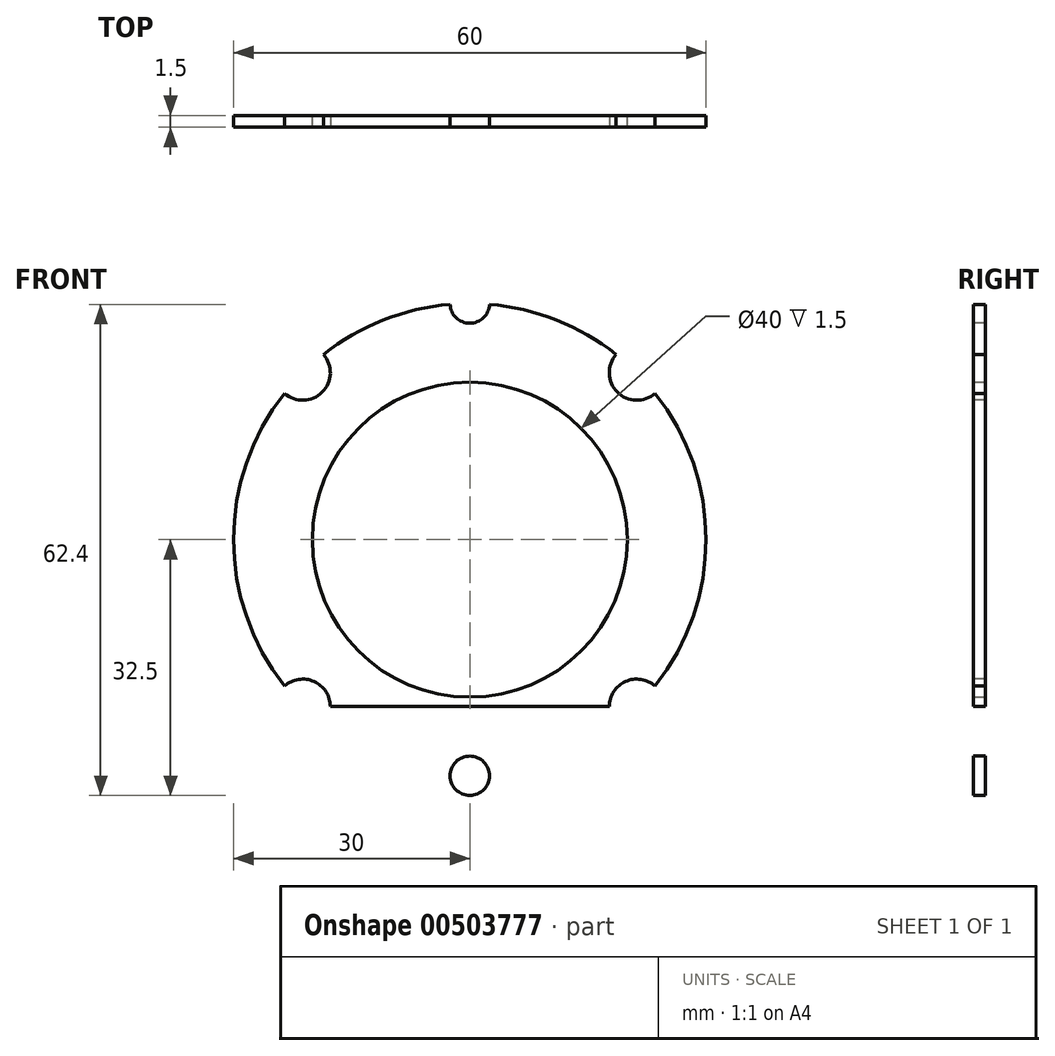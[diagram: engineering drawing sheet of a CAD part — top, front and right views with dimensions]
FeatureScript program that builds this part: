
annotation { "Feature Type Name" : "Feature", "Feature Type Description" : "" }
export const myFeature = defineFeature(function(context is Context, id is Id, definition is map)
    precondition{}
    {
        {
            var Q0;
            Q0=qCreatedBy(makeId("Front.planeOp"),FACE);
            var sketch = newSketch(context, id + "F0", { "sketchPlane" : qUnion([Q0])});
            skCircle(sketch, "E0", {"center": v(0, 0) * mm, "radius": 170.5 * mm});
            skCircle(sketch, "E1", {"center": v(0, 0) * mm, "radius": 20 * mm});
            skCircle(sketch, "E2.cCircle", {"center": v(0, 0) * mm, "radius": 21.21 * mm, "construction": true});
            skLineSegment(sketch, "E2.0", {"start": v(30, 0) * mm, "end": v(0, -30) * mm});
            skLineSegment(sketch, "E2.1", {"start": v(0, -30) * mm, "end": v(-30, 0) * mm});
            skLineSegment(sketch, "E2.2", {"start": v(-30, 0) * mm, "end": v(0, 30) * mm});
            skLineSegment(sketch, "E2.3", {"start": v(0, 30) * mm, "end": v(30, 0) * mm});
            skPoint(sketch, "E2.0.midPoint", {"position": v(15, -15) * mm});
            skLineSegment(sketch, "E3", {"start": v(0, 0) * mm, "end": v(21.21, -21.21) * mm});
            skLineSegment(sketch, "E4", {"start": v(0, 0) * mm, "end": v(-21.21, 21.21) * mm});
            skSolve(sketch);
        }
        {
            var Q0;
            {var subQ0=sQuery(id+"F0.wireOp",EDGE,"E2.3");Q0=makeQuery(id+"F0.imprint","IMPRINT",FACE,{"disambiguationData":[TD([[makeQuery(id+"F0.imprint","IMPRINT",EDGE,{"derivedFrom":subQ0}),-1.0]])]});}
            var Q1;
            {var subQ0=sQuery(id+"F0.wireOp",EDGE,"E2.1");Q1=makeQuery(id+"F0.imprint","IMPRINT",FACE,{"disambiguationData":[TD([[makeQuery(id+"F0.imprint","IMPRINT",EDGE,{"derivedFrom":subQ0}),-1.0]])]});}
            var Q2;
            Q2=makeQuery(id+"F0.imprint","IMPRINT",FACE,{"disambiguationData":[TD([[makeQuery(id+"F0.imprint","IMPRINT",EDGE,{"derivedFrom":sQuery(id+"F0.wireOp",EDGE,"E0")}),1.0]])]});
            extrude(context, id + "F1", {"entities" : qUnion([Q0, Q1, Q2]), "depth" : 1.5 * mm});
        }
        {
            var Q0;
            Q0=makeQuery(id+"F1.opExtrude","CAP_FACE",FACE,{"disambiguationData":[OSD([sQuery(id+"F0.wireOp",EDGE,"E0"),sQuery(id+"F0.wireOp",EDGE,"E1")])],"isStart":false});
            var sketch = newSketch(context, id + "F2", { "sketchPlane" : qUnion([Q0])});
            skCircle(sketch, "E5.cCircle", {"center": v(0, 0) * mm, "radius": 21.21 * mm, "construction": true});
            skLineSegment(sketch, "E5.0", {"start": v(-21.21, 21.21) * mm, "end": v(21.21, 21.21) * mm});
            skLineSegment(sketch, "E5.1", {"start": v(21.21, 21.21) * mm, "end": v(21.21, -21.21) * mm});
            skLineSegment(sketch, "E5.2", {"start": v(21.21, -21.21) * mm, "end": v(-21.21, -21.21) * mm});
            skLineSegment(sketch, "E5.3", {"start": v(-21.21, -21.21) * mm, "end": v(-21.21, 21.21) * mm});
            skPoint(sketch, "E5.0.midPoint", {"position": v(0, 21.21) * mm});
            skCircle(sketch, "E6", {"center": v(0, 0) * mm, "radius": 30 * mm});
            skPoint(sketch, "E7", {"position": v(0, 30) * mm});
            skPoint(sketch, "E8", {"position": v(0, -30) * mm});
            skCircle(sketch, "E9", {"center": v(0, 30) * mm, "radius": 2.5 * mm});
            skCircle(sketch, "E10", {"center": v(0, -30) * mm, "radius": 2.5 * mm});
            skCircle(sketch, "E11", {"center": v(21.21, 21.21) * mm, "radius": 3.5 * mm});
            skCircle(sketch, "E12", {"center": v(-21.21, 21.21) * mm, "radius": 3.5 * mm});
            skCircle(sketch, "E13", {"center": v(-21.21, -21.21) * mm, "radius": 3.5 * mm});
            skCircle(sketch, "E14", {"center": v(21.21, -21.21) * mm, "radius": 3.5 * mm});
            skSolve(sketch);
        }
        {
            var Q0;
            {var subQ1=sQuery(id+"F2.wireOp",EDGE,"E5.0");var subQ3=sQuery(id+"F2.wireOp",EDGE,"E12");var subQ4=makeQuery(id+"F2.imprint","INTERSECT",VERTEX,{"derivedFrom":[subQ1,subQ3]});Q0=makeQuery(id+"F2.imprint","IMPRINT",FACE,{"disambiguationData":[TD([[makeQuery(id+"F2.imprint","IMPRINT",EDGE,{"disambiguationData":[TD([[subQ4,1.0]])],"derivedFrom":subQ3}),1.0]])]});}
            var Q1;
            {var subQ0=sQuery(id+"F2.wireOp",EDGE,"E6");var subQ2=sQuery(id+"F2.wireOp",EDGE,"E12");var subQ3=makeQuery(id+"F2.imprint","INTERSECT",VERTEX,{"disambiguationData":[OD(0.0)],"derivedFrom":[subQ0,subQ2]});Q1=makeQuery(id+"F2.imprint","IMPRINT",FACE,{"disambiguationData":[TD([[makeQuery(id+"F2.imprint","IMPRINT",EDGE,{"disambiguationData":[TD([[subQ3,-1.0]])],"derivedFrom":subQ2}),1.0]])]});}
            var Q2;
            {var subQ1=sQuery(id+"F2.wireOp",EDGE,"E5.3");var subQ3=sQuery(id+"F2.wireOp",EDGE,"E12");var subQ4=makeQuery(id+"F2.imprint","INTERSECT",VERTEX,{"derivedFrom":[subQ1,subQ3]});Q2=makeQuery(id+"F2.imprint","IMPRINT",FACE,{"disambiguationData":[TD([[makeQuery(id+"F2.imprint","IMPRINT",EDGE,{"disambiguationData":[TD([[subQ4,1.0]])],"derivedFrom":subQ3}),1.0]])]});}
            var Q3;
            {var subQ1=sQuery(id+"F2.wireOp",EDGE,"E5.0");var subQ3=sQuery(id+"F2.wireOp",EDGE,"E12");var subQ4=makeQuery(id+"F2.imprint","INTERSECT",VERTEX,{"derivedFrom":[subQ1,subQ3]});Q3=makeQuery(id+"F2.imprint","IMPRINT",FACE,{"disambiguationData":[TD([[makeQuery(id+"F2.imprint","IMPRINT",EDGE,{"disambiguationData":[TD([[subQ4,-1.0]])],"derivedFrom":subQ3}),1.0]])]});}
            var Q4;
            {var subQ0=sQuery(id+"F2.wireOp",EDGE,"E6");var subQ2=sQuery(id+"F2.wireOp",EDGE,"E13");var subQ3=makeQuery(id+"F2.imprint","INTERSECT",VERTEX,{"disambiguationData":[OD(0.0)],"derivedFrom":[subQ0,subQ2]});Q4=makeQuery(id+"F2.imprint","IMPRINT",FACE,{"disambiguationData":[TD([[makeQuery(id+"F2.imprint","IMPRINT",EDGE,{"disambiguationData":[TD([[subQ3,-1.0]])],"derivedFrom":subQ2}),1.0]])]});}
            var Q5;
            {var subQ1=sQuery(id+"F2.wireOp",EDGE,"E5.3");var subQ3=sQuery(id+"F2.wireOp",EDGE,"E13");var subQ4=makeQuery(id+"F2.imprint","INTERSECT",VERTEX,{"derivedFrom":[subQ1,subQ3]});Q5=makeQuery(id+"F2.imprint","IMPRINT",FACE,{"disambiguationData":[TD([[makeQuery(id+"F2.imprint","IMPRINT",EDGE,{"disambiguationData":[TD([[subQ4,-1.0]])],"derivedFrom":subQ3}),1.0]])]});}
            var Q6;
            {var subQ1=sQuery(id+"F2.wireOp",EDGE,"E5.2");var subQ3=sQuery(id+"F2.wireOp",EDGE,"E13");var subQ4=makeQuery(id+"F2.imprint","INTERSECT",VERTEX,{"derivedFrom":[subQ1,subQ3]});Q6=makeQuery(id+"F2.imprint","IMPRINT",FACE,{"disambiguationData":[TD([[makeQuery(id+"F2.imprint","IMPRINT",EDGE,{"disambiguationData":[TD([[subQ4,-1.0]])],"derivedFrom":subQ3}),1.0]])]});}
            var Q7;
            {var subQ1=sQuery(id+"F2.wireOp",EDGE,"E5.2");var subQ3=sQuery(id+"F2.wireOp",EDGE,"E13");var subQ4=makeQuery(id+"F2.imprint","INTERSECT",VERTEX,{"derivedFrom":[subQ1,subQ3]});Q7=makeQuery(id+"F2.imprint","IMPRINT",FACE,{"disambiguationData":[TD([[makeQuery(id+"F2.imprint","IMPRINT",EDGE,{"disambiguationData":[TD([[subQ4,1.0]])],"derivedFrom":subQ3}),1.0]])]});}
            var Q8;
            {var subQ0=sQuery(id+"F2.wireOp",EDGE,"E10");var subQ1=sQuery(id+"F2.wireOp",EDGE,"E6");var subQ2=makeQuery(id+"F2.imprint","INTERSECT",VERTEX,{"disambiguationData":[OD(0.0)],"derivedFrom":[subQ1,subQ0]});Q8=makeQuery(id+"F2.imprint","IMPRINT",FACE,{"disambiguationData":[TD([[makeQuery(id+"F2.imprint","IMPRINT",EDGE,{"disambiguationData":[TD([[subQ2,-1.0]])],"derivedFrom":subQ1}),1.0]])]});}
            var Q9;
            {var subQ0=sQuery(id+"F2.wireOp",EDGE,"E10");var subQ1=sQuery(id+"F2.wireOp",EDGE,"E6");var subQ2=makeQuery(id+"F2.imprint","INTERSECT",VERTEX,{"disambiguationData":[OD(0.0)],"derivedFrom":[subQ1,subQ0]});Q9=makeQuery(id+"F2.imprint","IMPRINT",FACE,{"disambiguationData":[TD([[makeQuery(id+"F2.imprint","IMPRINT",EDGE,{"disambiguationData":[TD([[subQ2,-1.0]])],"derivedFrom":subQ1}),-1.0]])]});}
            var Q10;
            {var subQ0=sQuery(id+"F2.wireOp",EDGE,"E6");var subQ2=sQuery(id+"F2.wireOp",EDGE,"E14");var subQ3=makeQuery(id+"F2.imprint","INTERSECT",VERTEX,{"disambiguationData":[OD(0.0)],"derivedFrom":[subQ0,subQ2]});Q10=makeQuery(id+"F2.imprint","IMPRINT",FACE,{"disambiguationData":[TD([[makeQuery(id+"F2.imprint","IMPRINT",EDGE,{"disambiguationData":[TD([[subQ3,-1.0]])],"derivedFrom":subQ2}),1.0]])]});}
            var Q11;
            {var subQ1=sQuery(id+"F2.wireOp",EDGE,"E5.1");var subQ3=sQuery(id+"F2.wireOp",EDGE,"E14");var subQ4=makeQuery(id+"F2.imprint","INTERSECT",VERTEX,{"derivedFrom":[subQ1,subQ3]});Q11=makeQuery(id+"F2.imprint","IMPRINT",FACE,{"disambiguationData":[TD([[makeQuery(id+"F2.imprint","IMPRINT",EDGE,{"disambiguationData":[TD([[subQ4,-1.0]])],"derivedFrom":subQ3}),1.0]])]});}
            var Q12;
            {var subQ1=sQuery(id+"F2.wireOp",EDGE,"E5.2");var subQ3=sQuery(id+"F2.wireOp",EDGE,"E14");var subQ4=makeQuery(id+"F2.imprint","INTERSECT",VERTEX,{"derivedFrom":[subQ1,subQ3]});Q12=makeQuery(id+"F2.imprint","IMPRINT",FACE,{"disambiguationData":[TD([[makeQuery(id+"F2.imprint","IMPRINT",EDGE,{"disambiguationData":[TD([[subQ4,-1.0]])],"derivedFrom":subQ3}),1.0]])]});}
            var Q13;
            {var subQ1=sQuery(id+"F2.wireOp",EDGE,"E5.1");var subQ3=sQuery(id+"F2.wireOp",EDGE,"E14");var subQ4=makeQuery(id+"F2.imprint","INTERSECT",VERTEX,{"derivedFrom":[subQ1,subQ3]});Q13=makeQuery(id+"F2.imprint","IMPRINT",FACE,{"disambiguationData":[TD([[makeQuery(id+"F2.imprint","IMPRINT",EDGE,{"disambiguationData":[TD([[subQ4,1.0]])],"derivedFrom":subQ3}),1.0]])]});}
            var Q14;
            {var subQ1=sQuery(id+"F2.wireOp",EDGE,"E5.0");var subQ3=sQuery(id+"F2.wireOp",EDGE,"E11");var subQ4=makeQuery(id+"F2.imprint","INTERSECT",VERTEX,{"derivedFrom":[subQ1,subQ3]});Q14=makeQuery(id+"F2.imprint","IMPRINT",FACE,{"disambiguationData":[TD([[makeQuery(id+"F2.imprint","IMPRINT",EDGE,{"disambiguationData":[TD([[subQ4,-1.0]])],"derivedFrom":subQ3}),1.0]])]});}
            var Q15;
            {var subQ1=sQuery(id+"F2.wireOp",EDGE,"E5.0");var subQ3=sQuery(id+"F2.wireOp",EDGE,"E11");var subQ4=makeQuery(id+"F2.imprint","INTERSECT",VERTEX,{"derivedFrom":[subQ1,subQ3]});Q15=makeQuery(id+"F2.imprint","IMPRINT",FACE,{"disambiguationData":[TD([[makeQuery(id+"F2.imprint","IMPRINT",EDGE,{"disambiguationData":[TD([[subQ4,1.0]])],"derivedFrom":subQ3}),1.0]])]});}
            var Q16;
            {var subQ1=sQuery(id+"F2.wireOp",EDGE,"E5.1");var subQ3=sQuery(id+"F2.wireOp",EDGE,"E11");var subQ4=makeQuery(id+"F2.imprint","INTERSECT",VERTEX,{"derivedFrom":[subQ1,subQ3]});Q16=makeQuery(id+"F2.imprint","IMPRINT",FACE,{"disambiguationData":[TD([[makeQuery(id+"F2.imprint","IMPRINT",EDGE,{"disambiguationData":[TD([[subQ4,-1.0]])],"derivedFrom":subQ3}),1.0]])]});}
            var Q17;
            {var subQ0=sQuery(id+"F2.wireOp",EDGE,"E6");var subQ2=sQuery(id+"F2.wireOp",EDGE,"E11");var subQ3=makeQuery(id+"F2.imprint","INTERSECT",VERTEX,{"disambiguationData":[OD(0.0)],"derivedFrom":[subQ0,subQ2]});Q17=makeQuery(id+"F2.imprint","IMPRINT",FACE,{"disambiguationData":[TD([[makeQuery(id+"F2.imprint","IMPRINT",EDGE,{"disambiguationData":[TD([[subQ3,-1.0]])],"derivedFrom":subQ2}),1.0]])]});}
            var Q18;
            {var subQ0=sQuery(id+"F2.wireOp",EDGE,"E9");var subQ1=sQuery(id+"F2.wireOp",EDGE,"E6");var subQ2=makeQuery(id+"F2.imprint","INTERSECT",VERTEX,{"disambiguationData":[OD(0.0)],"derivedFrom":[subQ1,subQ0]});Q18=makeQuery(id+"F2.imprint","IMPRINT",FACE,{"disambiguationData":[TD([[makeQuery(id+"F2.imprint","IMPRINT",EDGE,{"disambiguationData":[TD([[subQ2,-1.0]])],"derivedFrom":subQ1}),1.0]])]});}
            var Q19;
            {var subQ0=sQuery(id+"F2.wireOp",EDGE,"E9");var subQ1=sQuery(id+"F2.wireOp",EDGE,"E6");var subQ2=makeQuery(id+"F2.imprint","INTERSECT",VERTEX,{"disambiguationData":[OD(0.0)],"derivedFrom":[subQ1,subQ0]});Q19=makeQuery(id+"F2.imprint","IMPRINT",FACE,{"disambiguationData":[TD([[makeQuery(id+"F2.imprint","IMPRINT",EDGE,{"disambiguationData":[TD([[subQ2,-1.0]])],"derivedFrom":subQ1}),-1.0]])]});}
            extrude(context, id + "F3", {"entities" : qUnion([Q0, Q1, Q2, Q3, Q4, Q5, Q6, Q7, Q8, Q9, Q10, Q11, Q12, Q13, Q14, Q15, Q16, Q17, Q18, Q19]), "operationType" : NewBodyOperationType.REMOVE, "oppositeDirection" : true, "depth" : 25 * mm});
        }
        {
            var Q0;
            Q0=makeQuery(id+"F1.opExtrude","CAP_FACE",FACE,{"disambiguationData":[OSD([sQuery(id+"F0.wireOp",EDGE,"E0"),sQuery(id+"F0.wireOp",EDGE,"E1")])],"isStart":false});
            var sketch = newSketch(context, id + "F4", { "sketchPlane" : qUnion([Q0])});
            skCircle(sketch, "E15.cCircle", {"center": v(0, 0) * mm, "radius": 92.39 * mm, "construction": true});
            skLineSegment(sketch, "E15.0", {"start": v(38.27, -92.39) * mm, "end": v(-38.27, -92.39) * mm});
            skLineSegment(sketch, "E15.1", {"start": v(-38.27, -92.39) * mm, "end": v(-92.39, -38.27) * mm});
            skLineSegment(sketch, "E15.2", {"start": v(-92.39, -38.27) * mm, "end": v(-92.39, 38.27) * mm});
            skLineSegment(sketch, "E15.3", {"start": v(-92.39, 38.27) * mm, "end": v(-38.27, 92.39) * mm});
            skLineSegment(sketch, "E15.4", {"start": v(-38.27, 92.39) * mm, "end": v(38.27, 92.39) * mm});
            skLineSegment(sketch, "E15.5", {"start": v(38.27, 92.39) * mm, "end": v(92.39, 38.27) * mm});
            skLineSegment(sketch, "E15.6", {"start": v(92.39, 38.27) * mm, "end": v(92.39, -38.27) * mm});
            skLineSegment(sketch, "E15.7", {"start": v(92.39, -38.27) * mm, "end": v(38.27, -92.39) * mm});
            skPoint(sketch, "E15.0.midPoint", {"position": v(0, -92.39) * mm});
            skCircle(sketch, "E16", {"center": v(-38.27, 92.39) * mm, "radius": 12.5 * mm});
            skCircle(sketch, "E17", {"center": v(38.27, 92.39) * mm, "radius": 12.5 * mm});
            skCircle(sketch, "E18", {"center": v(92.39, 38.27) * mm, "radius": 12.5 * mm});
            skCircle(sketch, "E19", {"center": v(92.39, -38.27) * mm, "radius": 12.5 * mm});
            skCircle(sketch, "E20", {"center": v(38.27, -92.39) * mm, "radius": 12.5 * mm});
            skCircle(sketch, "E21", {"center": v(-38.27, -92.39) * mm, "radius": 12.5 * mm});
            skCircle(sketch, "E22", {"center": v(-92.39, -38.27) * mm, "radius": 12.5 * mm});
            skCircle(sketch, "E23", {"center": v(-92.39, 38.27) * mm, "radius": 12.5 * mm});
            skSolve(sketch);
        }
        {
            var Q0;
            {var subQ0=sQuery(id+"F4.wireOp",EDGE,"E15.3");var subQ1=sQuery(id+"F4.wireOp",EDGE,"E15.2");var subQ2=makeQuery(id+"F4.imprint","INTERSECT",VERTEX,{"derivedFrom":[subQ1,subQ0]});Q0=makeQuery(id+"F4.imprint","IMPRINT",FACE,{"disambiguationData":[TD([[makeQuery(id+"F4.imprint","IMPRINT",EDGE,{"disambiguationData":[TD([[subQ2,1.0]])],"derivedFrom":subQ1}),-1.0]])]});}
            var Q1;
            {var subQ0=sQuery(id+"F4.wireOp",EDGE,"E15.3");var subQ1=sQuery(id+"F4.wireOp",EDGE,"E15.2");var subQ2=makeQuery(id+"F4.imprint","INTERSECT",VERTEX,{"derivedFrom":[subQ1,subQ0]});Q1=makeQuery(id+"F4.imprint","IMPRINT",FACE,{"disambiguationData":[TD([[makeQuery(id+"F4.imprint","IMPRINT",EDGE,{"disambiguationData":[TD([[subQ2,1.0]])],"derivedFrom":subQ1}),1.0]])]});}
            var Q2;
            {var subQ0=sQuery(id+"F4.wireOp",EDGE,"E15.2");var subQ1=sQuery(id+"F4.wireOp",EDGE,"E15.1");var subQ2=makeQuery(id+"F4.imprint","INTERSECT",VERTEX,{"derivedFrom":[subQ1,subQ0]});Q2=makeQuery(id+"F4.imprint","IMPRINT",FACE,{"disambiguationData":[TD([[makeQuery(id+"F4.imprint","IMPRINT",EDGE,{"disambiguationData":[TD([[subQ2,1.0]])],"derivedFrom":subQ1}),-1.0]])]});}
            var Q3;
            {var subQ0=sQuery(id+"F4.wireOp",EDGE,"E15.2");var subQ1=sQuery(id+"F4.wireOp",EDGE,"E15.1");var subQ2=makeQuery(id+"F4.imprint","INTERSECT",VERTEX,{"derivedFrom":[subQ1,subQ0]});Q3=makeQuery(id+"F4.imprint","IMPRINT",FACE,{"disambiguationData":[TD([[makeQuery(id+"F4.imprint","IMPRINT",EDGE,{"disambiguationData":[TD([[subQ2,1.0]])],"derivedFrom":subQ1}),1.0]])]});}
            var Q4;
            {var subQ0=sQuery(id+"F4.wireOp",EDGE,"E15.1");var subQ1=sQuery(id+"F4.wireOp",EDGE,"E15.0");var subQ2=makeQuery(id+"F4.imprint","INTERSECT",VERTEX,{"derivedFrom":[subQ1,subQ0]});Q4=makeQuery(id+"F4.imprint","IMPRINT",FACE,{"disambiguationData":[TD([[makeQuery(id+"F4.imprint","IMPRINT",EDGE,{"disambiguationData":[TD([[subQ2,1.0]])],"derivedFrom":subQ1}),-1.0]])]});}
            var Q5;
            {var subQ0=sQuery(id+"F4.wireOp",EDGE,"E15.1");var subQ1=sQuery(id+"F4.wireOp",EDGE,"E15.0");var subQ2=makeQuery(id+"F4.imprint","INTERSECT",VERTEX,{"derivedFrom":[subQ1,subQ0]});Q5=makeQuery(id+"F4.imprint","IMPRINT",FACE,{"disambiguationData":[TD([[makeQuery(id+"F4.imprint","IMPRINT",EDGE,{"disambiguationData":[TD([[subQ2,1.0]])],"derivedFrom":subQ1}),1.0]])]});}
            var Q6;
            {var subQ0=sQuery(id+"F4.wireOp",EDGE,"E15.7");var subQ1=sQuery(id+"F4.wireOp",EDGE,"E15.0");var subQ2=makeQuery(id+"F4.imprint","INTERSECT",VERTEX,{"derivedFrom":[subQ1,subQ0]});Q6=makeQuery(id+"F4.imprint","IMPRINT",FACE,{"disambiguationData":[TD([[makeQuery(id+"F4.imprint","IMPRINT",EDGE,{"disambiguationData":[TD([[subQ2,-1.0]])],"derivedFrom":subQ1}),-1.0]])]});}
            var Q7;
            {var subQ0=sQuery(id+"F4.wireOp",EDGE,"E15.7");var subQ1=sQuery(id+"F4.wireOp",EDGE,"E15.0");var subQ2=makeQuery(id+"F4.imprint","INTERSECT",VERTEX,{"derivedFrom":[subQ1,subQ0]});Q7=makeQuery(id+"F4.imprint","IMPRINT",FACE,{"disambiguationData":[TD([[makeQuery(id+"F4.imprint","IMPRINT",EDGE,{"disambiguationData":[TD([[subQ2,-1.0]])],"derivedFrom":subQ1}),1.0]])]});}
            var Q8;
            {var subQ0=sQuery(id+"F4.wireOp",EDGE,"E15.7");var subQ1=sQuery(id+"F4.wireOp",EDGE,"E15.6");var subQ2=makeQuery(id+"F4.imprint","INTERSECT",VERTEX,{"derivedFrom":[subQ1,subQ0]});Q8=makeQuery(id+"F4.imprint","IMPRINT",FACE,{"disambiguationData":[TD([[makeQuery(id+"F4.imprint","IMPRINT",EDGE,{"disambiguationData":[TD([[subQ2,1.0]])],"derivedFrom":subQ1}),-1.0]])]});}
            var Q9;
            {var subQ0=sQuery(id+"F4.wireOp",EDGE,"E15.7");var subQ1=sQuery(id+"F4.wireOp",EDGE,"E15.6");var subQ2=makeQuery(id+"F4.imprint","INTERSECT",VERTEX,{"derivedFrom":[subQ1,subQ0]});Q9=makeQuery(id+"F4.imprint","IMPRINT",FACE,{"disambiguationData":[TD([[makeQuery(id+"F4.imprint","IMPRINT",EDGE,{"disambiguationData":[TD([[subQ2,1.0]])],"derivedFrom":subQ1}),1.0]])]});}
            var Q10;
            {var subQ0=sQuery(id+"F4.wireOp",EDGE,"E15.6");var subQ1=sQuery(id+"F4.wireOp",EDGE,"E15.5");var subQ2=makeQuery(id+"F4.imprint","INTERSECT",VERTEX,{"derivedFrom":[subQ1,subQ0]});Q10=makeQuery(id+"F4.imprint","IMPRINT",FACE,{"disambiguationData":[TD([[makeQuery(id+"F4.imprint","IMPRINT",EDGE,{"disambiguationData":[TD([[subQ2,1.0]])],"derivedFrom":subQ1}),-1.0]])]});}
            var Q11;
            {var subQ0=sQuery(id+"F4.wireOp",EDGE,"E15.6");var subQ1=sQuery(id+"F4.wireOp",EDGE,"E15.5");var subQ2=makeQuery(id+"F4.imprint","INTERSECT",VERTEX,{"derivedFrom":[subQ1,subQ0]});Q11=makeQuery(id+"F4.imprint","IMPRINT",FACE,{"disambiguationData":[TD([[makeQuery(id+"F4.imprint","IMPRINT",EDGE,{"disambiguationData":[TD([[subQ2,1.0]])],"derivedFrom":subQ1}),1.0]])]});}
            var Q12;
            {var subQ0=sQuery(id+"F4.wireOp",EDGE,"E15.5");var subQ1=sQuery(id+"F4.wireOp",EDGE,"E15.4");var subQ2=makeQuery(id+"F4.imprint","INTERSECT",VERTEX,{"derivedFrom":[subQ1,subQ0]});Q12=makeQuery(id+"F4.imprint","IMPRINT",FACE,{"disambiguationData":[TD([[makeQuery(id+"F4.imprint","IMPRINT",EDGE,{"disambiguationData":[TD([[subQ2,1.0]])],"derivedFrom":subQ1}),-1.0]])]});}
            var Q13;
            {var subQ0=sQuery(id+"F4.wireOp",EDGE,"E15.5");var subQ1=sQuery(id+"F4.wireOp",EDGE,"E15.4");var subQ2=makeQuery(id+"F4.imprint","INTERSECT",VERTEX,{"derivedFrom":[subQ1,subQ0]});Q13=makeQuery(id+"F4.imprint","IMPRINT",FACE,{"disambiguationData":[TD([[makeQuery(id+"F4.imprint","IMPRINT",EDGE,{"disambiguationData":[TD([[subQ2,1.0]])],"derivedFrom":subQ1}),1.0]])]});}
            var Q14;
            {var subQ0=sQuery(id+"F4.wireOp",EDGE,"E15.4");var subQ1=sQuery(id+"F4.wireOp",EDGE,"E15.3");var subQ2=makeQuery(id+"F4.imprint","INTERSECT",VERTEX,{"derivedFrom":[subQ1,subQ0]});Q14=makeQuery(id+"F4.imprint","IMPRINT",FACE,{"disambiguationData":[TD([[makeQuery(id+"F4.imprint","IMPRINT",EDGE,{"disambiguationData":[TD([[subQ2,1.0]])],"derivedFrom":subQ1}),-1.0]])]});}
            var Q15;
            {var subQ0=sQuery(id+"F4.wireOp",EDGE,"E15.4");var subQ1=sQuery(id+"F4.wireOp",EDGE,"E15.3");var subQ2=makeQuery(id+"F4.imprint","INTERSECT",VERTEX,{"derivedFrom":[subQ1,subQ0]});Q15=makeQuery(id+"F4.imprint","IMPRINT",FACE,{"disambiguationData":[TD([[makeQuery(id+"F4.imprint","IMPRINT",EDGE,{"disambiguationData":[TD([[subQ2,1.0]])],"derivedFrom":subQ1}),1.0]])]});}
            extrude(context, id + "F5", {"entities" : qUnion([Q0, Q1, Q2, Q3, Q4, Q5, Q6, Q7, Q8, Q9, Q10, Q11, Q12, Q13, Q14, Q15]), "operationType" : NewBodyOperationType.REMOVE, "oppositeDirection" : true, "depth" : 25 * mm});
        }
        {
            var Q0;
            Q0=makeQuery(id+"F1.opExtrude","CAP_FACE",FACE,{"disambiguationData":[OSD([sQuery(id+"F0.wireOp",EDGE,"E0"),sQuery(id+"F0.wireOp",EDGE,"E1")])],"isStart":false});
            var sketch = newSketch(context, id + "F6", { "sketchPlane" : qUnion([Q0])});
            skCircle(sketch, "E24", {"center": v(0, 0) * mm, "radius": 125 * mm});
            skPoint(sketch, "E25", {"position": v(0, 125) * mm});
            skPoint(sketch, "E26", {"position": v(2.5, 124.98) * mm});
            skPoint(sketch, "E27", {"position": v(-2.5, 124.97) * mm});
            skPoint(sketch, "E28", {"position": v(-2.5, 139.98) * mm});
            skPoint(sketch, "E29", {"position": v(2.5, 139.98) * mm});
            skLineSegment(sketch, "E30.bottom", {"start": v(-2.5, 139.98) * mm, "end": v(2.5, 139.98) * mm});
            skLineSegment(sketch, "E30.top", {"start": v(-2.5, 124.98) * mm, "end": v(2.5, 124.98) * mm});
            skLineSegment(sketch, "E30.left", {"start": v(-2.5, 139.98) * mm, "end": v(-2.5, 124.98) * mm});
            skLineSegment(sketch, "E30.right", {"start": v(2.5, 139.98) * mm, "end": v(2.5, 124.98) * mm});
            skLineSegment(sketch, "E31.1.0", {"start": v(-9.7, 139.66) * mm, "end": v(-8.4, 124.72) * mm});
            skLineSegment(sketch, "E31.1.1", {"start": v(-14.7, 139.22) * mm, "end": v(-13.38, 124.28) * mm});
            skLineSegment(sketch, "E31.1.2", {"start": v(-14.7, 139.22) * mm, "end": v(-9.7, 139.66) * mm});
            skLineSegment(sketch, "E31.1.4", {"start": v(-13.38, 124.28) * mm, "end": v(-8.4, 124.72) * mm});
            skLineSegment(sketch, "E31.2.0", {"start": v(-21.84, 138.28) * mm, "end": v(-19.24, 123.51) * mm});
            skLineSegment(sketch, "E31.2.1", {"start": v(-26.77, 137.41) * mm, "end": v(-24.16, 122.64) * mm});
            skLineSegment(sketch, "E31.2.2", {"start": v(-26.77, 137.41) * mm, "end": v(-21.84, 138.28) * mm});
            skLineSegment(sketch, "E31.2.4", {"start": v(-24.16, 122.64) * mm, "end": v(-19.24, 123.51) * mm});
            skLineSegment(sketch, "E31.3.0", {"start": v(-33.81, 135.85) * mm, "end": v(-29.93, 121.36) * mm});
            skLineSegment(sketch, "E31.3.1", {"start": v(-38.64, 134.56) * mm, "end": v(-34.76, 120.07) * mm});
            skLineSegment(sketch, "E31.3.2", {"start": v(-38.64, 134.56) * mm, "end": v(-33.81, 135.85) * mm});
            skLineSegment(sketch, "E31.3.4", {"start": v(-34.76, 120.07) * mm, "end": v(-29.93, 121.36) * mm});
            skLineSegment(sketch, "E31.4.0", {"start": v(-45.53, 132.39) * mm, "end": v(-40.4, 118.3) * mm});
            skLineSegment(sketch, "E31.4.1", {"start": v(-50.22, 130.68) * mm, "end": v(-45.1, 116.58) * mm});
            skLineSegment(sketch, "E31.4.2", {"start": v(-50.22, 130.68) * mm, "end": v(-45.53, 132.39) * mm});
            skLineSegment(sketch, "E31.4.4", {"start": v(-45.1, 116.58) * mm, "end": v(-40.4, 118.3) * mm});
            skLineSegment(sketch, "E31.5.0", {"start": v(-56.9, 127.92) * mm, "end": v(-50.55, 114.32) * mm});
            skLineSegment(sketch, "E31.5.1", {"start": v(-61.42, 125.8) * mm, "end": v(-55.08, 112.2) * mm});
            skLineSegment(sketch, "E31.5.2", {"start": v(-61.42, 125.8) * mm, "end": v(-56.9, 127.92) * mm});
            skLineSegment(sketch, "E31.5.4", {"start": v(-55.08, 112.2) * mm, "end": v(-50.55, 114.32) * mm});
            skLineSegment(sketch, "E31.6.0", {"start": v(-67.82, 122.47) * mm, "end": v(-60.32, 109.48) * mm});
            skLineSegment(sketch, "E31.6.1", {"start": v(-72.15, 119.97) * mm, "end": v(-64.65, 106.98) * mm});
            skLineSegment(sketch, "E31.6.2", {"start": v(-72.15, 119.97) * mm, "end": v(-67.82, 122.47) * mm});
            skLineSegment(sketch, "E31.6.4", {"start": v(-64.65, 106.98) * mm, "end": v(-60.32, 109.48) * mm});
            skLineSegment(sketch, "E31.7.0", {"start": v(-78.24, 116.1) * mm, "end": v(-69.63, 103.8) * mm});
            skLineSegment(sketch, "E31.7.1", {"start": v(-82.33, 113.23) * mm, "end": v(-73.73, 100.94) * mm});
            skLineSegment(sketch, "E31.7.2", {"start": v(-82.33, 113.23) * mm, "end": v(-78.24, 116.1) * mm});
            skLineSegment(sketch, "E31.7.4", {"start": v(-73.73, 100.94) * mm, "end": v(-69.63, 103.8) * mm});
            skLineSegment(sketch, "E31.8.0", {"start": v(-88.06, 108.83) * mm, "end": v(-78.42, 97.34) * mm});
            skLineSegment(sketch, "E31.8.1", {"start": v(-91.89, 105.62) * mm, "end": v(-82.25, 94.13) * mm});
            skLineSegment(sketch, "E31.8.2", {"start": v(-91.89, 105.62) * mm, "end": v(-88.06, 108.83) * mm});
            skLineSegment(sketch, "E31.8.4", {"start": v(-82.25, 94.13) * mm, "end": v(-78.42, 97.34) * mm});
            skLineSegment(sketch, "E31.9.0", {"start": v(-97.2, 100.74) * mm, "end": v(-86.6, 90.14) * mm});
            skLineSegment(sketch, "E31.9.1", {"start": v(-100.75, 97.2) * mm, "end": v(-90.14, 86.6) * mm});
            skLineSegment(sketch, "E31.9.2", {"start": v(-100.75, 97.2) * mm, "end": v(-97.2, 100.74) * mm});
            skLineSegment(sketch, "E31.9.4", {"start": v(-90.14, 86.6) * mm, "end": v(-86.6, 90.14) * mm});
            skLineSegment(sketch, "E31.10.0", {"start": v(-105.62, 91.89) * mm, "end": v(-94.13, 82.25) * mm});
            skLineSegment(sketch, "E31.10.1", {"start": v(-108.83, 88.06) * mm, "end": v(-97.34, 78.42) * mm});
            skLineSegment(sketch, "E31.10.2", {"start": v(-108.83, 88.06) * mm, "end": v(-105.62, 91.89) * mm});
            skLineSegment(sketch, "E31.10.4", {"start": v(-97.34, 78.42) * mm, "end": v(-94.13, 82.25) * mm});
            skLineSegment(sketch, "E31.11.0", {"start": v(-113.23, 82.33) * mm, "end": v(-100.94, 73.73) * mm});
            skLineSegment(sketch, "E31.11.1", {"start": v(-116.1, 78.24) * mm, "end": v(-103.8, 69.63) * mm});
            skLineSegment(sketch, "E31.11.2", {"start": v(-116.1, 78.24) * mm, "end": v(-113.23, 82.33) * mm});
            skLineSegment(sketch, "E31.11.4", {"start": v(-103.8, 69.63) * mm, "end": v(-100.94, 73.73) * mm});
            skLineSegment(sketch, "E31.12.0", {"start": v(-119.97, 72.15) * mm, "end": v(-106.98, 64.65) * mm});
            skLineSegment(sketch, "E31.12.1", {"start": v(-122.47, 67.82) * mm, "end": v(-109.48, 60.32) * mm});
            skLineSegment(sketch, "E31.12.2", {"start": v(-122.47, 67.82) * mm, "end": v(-119.97, 72.15) * mm});
            skLineSegment(sketch, "E31.12.4", {"start": v(-109.48, 60.32) * mm, "end": v(-106.98, 64.65) * mm});
            skLineSegment(sketch, "E31.13.0", {"start": v(-125.8, 61.42) * mm, "end": v(-112.2, 55.08) * mm});
            skLineSegment(sketch, "E31.13.1", {"start": v(-127.92, 56.9) * mm, "end": v(-114.32, 50.55) * mm});
            skLineSegment(sketch, "E31.13.2", {"start": v(-127.92, 56.9) * mm, "end": v(-125.8, 61.42) * mm});
            skLineSegment(sketch, "E31.13.4", {"start": v(-114.32, 50.55) * mm, "end": v(-112.2, 55.08) * mm});
            skLineSegment(sketch, "E31.14.0", {"start": v(-130.68, 50.22) * mm, "end": v(-116.58, 45.1) * mm});
            skLineSegment(sketch, "E31.14.1", {"start": v(-132.39, 45.53) * mm, "end": v(-118.3, 40.4) * mm});
            skLineSegment(sketch, "E31.14.2", {"start": v(-132.39, 45.53) * mm, "end": v(-130.68, 50.22) * mm});
            skLineSegment(sketch, "E31.14.4", {"start": v(-118.3, 40.4) * mm, "end": v(-116.58, 45.1) * mm});
            skLineSegment(sketch, "E31.15.0", {"start": v(-134.56, 38.64) * mm, "end": v(-120.07, 34.76) * mm});
            skLineSegment(sketch, "E31.15.1", {"start": v(-135.85, 33.81) * mm, "end": v(-121.36, 29.93) * mm});
            skLineSegment(sketch, "E31.15.2", {"start": v(-135.85, 33.81) * mm, "end": v(-134.56, 38.64) * mm});
            skLineSegment(sketch, "E31.15.4", {"start": v(-121.36, 29.93) * mm, "end": v(-120.07, 34.76) * mm});
            skLineSegment(sketch, "E31.16.0", {"start": v(-137.41, 26.77) * mm, "end": v(-122.64, 24.16) * mm});
            skLineSegment(sketch, "E31.16.1", {"start": v(-138.28, 21.84) * mm, "end": v(-123.51, 19.24) * mm});
            skLineSegment(sketch, "E31.16.2", {"start": v(-138.28, 21.84) * mm, "end": v(-137.41, 26.77) * mm});
            skLineSegment(sketch, "E31.16.4", {"start": v(-123.51, 19.24) * mm, "end": v(-122.64, 24.16) * mm});
            skLineSegment(sketch, "E31.17.0", {"start": v(-139.22, 14.69) * mm, "end": v(-124.28, 13.38) * mm});
            skLineSegment(sketch, "E31.17.1", {"start": v(-139.66, 9.7) * mm, "end": v(-124.72, 8.4) * mm});
            skLineSegment(sketch, "E31.17.2", {"start": v(-139.66, 9.7) * mm, "end": v(-139.22, 14.69) * mm});
            skLineSegment(sketch, "E31.17.4", {"start": v(-124.72, 8.4) * mm, "end": v(-124.28, 13.38) * mm});
            skLineSegment(sketch, "E31.18.0", {"start": v(-139.98, 2.5) * mm, "end": v(-124.98, 2.5) * mm});
            skLineSegment(sketch, "E31.18.1", {"start": v(-139.98, -2.5) * mm, "end": v(-124.98, -2.5) * mm});
            skLineSegment(sketch, "E31.18.2", {"start": v(-139.98, -2.5) * mm, "end": v(-139.98, 2.5) * mm});
            skLineSegment(sketch, "E31.18.4", {"start": v(-124.98, -2.5) * mm, "end": v(-124.98, 2.5) * mm});
            skLineSegment(sketch, "E31.19.0", {"start": v(-139.66, -9.7) * mm, "end": v(-124.72, -8.4) * mm});
            skLineSegment(sketch, "E31.19.1", {"start": v(-139.22, -14.7) * mm, "end": v(-124.28, -13.38) * mm});
            skLineSegment(sketch, "E31.19.2", {"start": v(-139.22, -14.7) * mm, "end": v(-139.66, -9.7) * mm});
            skLineSegment(sketch, "E31.19.4", {"start": v(-124.28, -13.38) * mm, "end": v(-124.72, -8.4) * mm});
            skLineSegment(sketch, "E31.20.0", {"start": v(-138.28, -21.84) * mm, "end": v(-123.51, -19.24) * mm});
            skLineSegment(sketch, "E31.20.1", {"start": v(-137.41, -26.77) * mm, "end": v(-122.64, -24.16) * mm});
            skLineSegment(sketch, "E31.20.2", {"start": v(-137.41, -26.77) * mm, "end": v(-138.28, -21.84) * mm});
            skLineSegment(sketch, "E31.20.4", {"start": v(-122.64, -24.16) * mm, "end": v(-123.51, -19.24) * mm});
            skLineSegment(sketch, "E31.21.0", {"start": v(-135.85, -33.81) * mm, "end": v(-121.36, -29.93) * mm});
            skLineSegment(sketch, "E31.21.1", {"start": v(-134.56, -38.64) * mm, "end": v(-120.07, -34.76) * mm});
            skLineSegment(sketch, "E31.21.2", {"start": v(-134.56, -38.64) * mm, "end": v(-135.85, -33.81) * mm});
            skLineSegment(sketch, "E31.21.4", {"start": v(-120.07, -34.76) * mm, "end": v(-121.36, -29.93) * mm});
            skLineSegment(sketch, "E31.22.0", {"start": v(-132.39, -45.53) * mm, "end": v(-118.3, -40.4) * mm});
            skLineSegment(sketch, "E31.22.1", {"start": v(-130.68, -50.22) * mm, "end": v(-116.58, -45.1) * mm});
            skLineSegment(sketch, "E31.22.2", {"start": v(-130.68, -50.22) * mm, "end": v(-132.39, -45.53) * mm});
            skLineSegment(sketch, "E31.22.4", {"start": v(-116.58, -45.1) * mm, "end": v(-118.3, -40.4) * mm});
            skLineSegment(sketch, "E31.23.0", {"start": v(-127.92, -56.9) * mm, "end": v(-114.32, -50.55) * mm});
            skLineSegment(sketch, "E31.23.1", {"start": v(-125.8, -61.42) * mm, "end": v(-112.2, -55.08) * mm});
            skLineSegment(sketch, "E31.23.2", {"start": v(-125.8, -61.42) * mm, "end": v(-127.92, -56.9) * mm});
            skLineSegment(sketch, "E31.23.4", {"start": v(-112.2, -55.08) * mm, "end": v(-114.32, -50.55) * mm});
            skLineSegment(sketch, "E31.24.0", {"start": v(-122.47, -67.82) * mm, "end": v(-109.48, -60.32) * mm});
            skLineSegment(sketch, "E31.24.1", {"start": v(-119.97, -72.15) * mm, "end": v(-106.98, -64.65) * mm});
            skLineSegment(sketch, "E31.24.2", {"start": v(-119.97, -72.15) * mm, "end": v(-122.47, -67.82) * mm});
            skLineSegment(sketch, "E31.24.4", {"start": v(-106.98, -64.65) * mm, "end": v(-109.48, -60.32) * mm});
            skLineSegment(sketch, "E31.25.0", {"start": v(-116.1, -78.24) * mm, "end": v(-103.8, -69.63) * mm});
            skLineSegment(sketch, "E31.25.1", {"start": v(-113.23, -82.33) * mm, "end": v(-100.94, -73.73) * mm});
            skLineSegment(sketch, "E31.25.2", {"start": v(-113.23, -82.33) * mm, "end": v(-116.1, -78.24) * mm});
            skLineSegment(sketch, "E31.25.4", {"start": v(-100.94, -73.73) * mm, "end": v(-103.8, -69.63) * mm});
            skLineSegment(sketch, "E31.26.0", {"start": v(-108.83, -88.06) * mm, "end": v(-97.34, -78.42) * mm});
            skLineSegment(sketch, "E31.26.1", {"start": v(-105.62, -91.89) * mm, "end": v(-94.13, -82.25) * mm});
            skLineSegment(sketch, "E31.26.2", {"start": v(-105.62, -91.89) * mm, "end": v(-108.83, -88.06) * mm});
            skLineSegment(sketch, "E31.26.4", {"start": v(-94.13, -82.25) * mm, "end": v(-97.34, -78.42) * mm});
            skLineSegment(sketch, "E31.27.0", {"start": v(-100.74, -97.2) * mm, "end": v(-90.14, -86.6) * mm});
            skLineSegment(sketch, "E31.27.1", {"start": v(-97.2, -100.75) * mm, "end": v(-86.6, -90.14) * mm});
            skLineSegment(sketch, "E31.27.2", {"start": v(-97.2, -100.75) * mm, "end": v(-100.74, -97.2) * mm});
            skLineSegment(sketch, "E31.27.4", {"start": v(-86.6, -90.14) * mm, "end": v(-90.14, -86.6) * mm});
            skLineSegment(sketch, "E31.28.0", {"start": v(-91.89, -105.62) * mm, "end": v(-82.25, -94.13) * mm});
            skLineSegment(sketch, "E31.28.1", {"start": v(-88.06, -108.83) * mm, "end": v(-78.42, -97.34) * mm});
            skLineSegment(sketch, "E31.28.2", {"start": v(-88.06, -108.83) * mm, "end": v(-91.89, -105.62) * mm});
            skLineSegment(sketch, "E31.28.4", {"start": v(-78.42, -97.34) * mm, "end": v(-82.25, -94.13) * mm});
            skLineSegment(sketch, "E31.29.0", {"start": v(-82.33, -113.23) * mm, "end": v(-73.73, -100.94) * mm});
            skLineSegment(sketch, "E31.29.1", {"start": v(-78.24, -116.1) * mm, "end": v(-69.63, -103.8) * mm});
            skLineSegment(sketch, "E31.29.2", {"start": v(-78.24, -116.1) * mm, "end": v(-82.33, -113.23) * mm});
            skLineSegment(sketch, "E31.29.4", {"start": v(-69.63, -103.8) * mm, "end": v(-73.73, -100.94) * mm});
            skLineSegment(sketch, "E31.30.0", {"start": v(-72.15, -119.97) * mm, "end": v(-64.65, -106.98) * mm});
            skLineSegment(sketch, "E31.30.1", {"start": v(-67.82, -122.47) * mm, "end": v(-60.32, -109.48) * mm});
            skLineSegment(sketch, "E31.30.2", {"start": v(-67.82, -122.47) * mm, "end": v(-72.15, -119.97) * mm});
            skLineSegment(sketch, "E31.30.4", {"start": v(-60.32, -109.48) * mm, "end": v(-64.65, -106.98) * mm});
            skLineSegment(sketch, "E31.31.0", {"start": v(-61.42, -125.8) * mm, "end": v(-55.08, -112.2) * mm});
            skLineSegment(sketch, "E31.31.1", {"start": v(-56.9, -127.92) * mm, "end": v(-50.55, -114.32) * mm});
            skLineSegment(sketch, "E31.31.2", {"start": v(-56.9, -127.92) * mm, "end": v(-61.42, -125.8) * mm});
            skLineSegment(sketch, "E31.31.4", {"start": v(-50.55, -114.32) * mm, "end": v(-55.08, -112.2) * mm});
            skLineSegment(sketch, "E31.32.0", {"start": v(-50.22, -130.68) * mm, "end": v(-45.1, -116.58) * mm});
            skLineSegment(sketch, "E31.32.1", {"start": v(-45.53, -132.39) * mm, "end": v(-40.4, -118.3) * mm});
            skLineSegment(sketch, "E31.32.2", {"start": v(-45.53, -132.39) * mm, "end": v(-50.22, -130.68) * mm});
            skLineSegment(sketch, "E31.32.4", {"start": v(-40.4, -118.3) * mm, "end": v(-45.1, -116.58) * mm});
            skLineSegment(sketch, "E31.33.0", {"start": v(-38.64, -134.56) * mm, "end": v(-34.76, -120.07) * mm});
            skLineSegment(sketch, "E31.33.1", {"start": v(-33.81, -135.85) * mm, "end": v(-29.93, -121.36) * mm});
            skLineSegment(sketch, "E31.33.2", {"start": v(-33.81, -135.85) * mm, "end": v(-38.64, -134.56) * mm});
            skLineSegment(sketch, "E31.33.4", {"start": v(-29.93, -121.36) * mm, "end": v(-34.76, -120.07) * mm});
            skLineSegment(sketch, "E31.34.0", {"start": v(-26.77, -137.41) * mm, "end": v(-24.16, -122.64) * mm});
            skLineSegment(sketch, "E31.34.1", {"start": v(-21.84, -138.28) * mm, "end": v(-19.24, -123.51) * mm});
            skLineSegment(sketch, "E31.34.2", {"start": v(-21.84, -138.28) * mm, "end": v(-26.77, -137.41) * mm});
            skLineSegment(sketch, "E31.34.4", {"start": v(-19.24, -123.51) * mm, "end": v(-24.16, -122.64) * mm});
            skLineSegment(sketch, "E31.35.0", {"start": v(-14.69, -139.22) * mm, "end": v(-13.38, -124.28) * mm});
            skLineSegment(sketch, "E31.35.1", {"start": v(-9.7, -139.66) * mm, "end": v(-8.4, -124.72) * mm});
            skLineSegment(sketch, "E31.35.2", {"start": v(-9.7, -139.66) * mm, "end": v(-14.69, -139.22) * mm});
            skLineSegment(sketch, "E31.35.4", {"start": v(-8.4, -124.72) * mm, "end": v(-13.38, -124.28) * mm});
            skLineSegment(sketch, "E31.36.0", {"start": v(-2.5, -139.98) * mm, "end": v(-2.5, -124.98) * mm});
            skLineSegment(sketch, "E31.36.1", {"start": v(2.5, -139.98) * mm, "end": v(2.5, -124.98) * mm});
            skLineSegment(sketch, "E31.36.2", {"start": v(2.5, -139.98) * mm, "end": v(-2.5, -139.98) * mm});
            skLineSegment(sketch, "E31.36.4", {"start": v(2.5, -124.98) * mm, "end": v(-2.5, -124.98) * mm});
            skLineSegment(sketch, "E31.37.0", {"start": v(9.7, -139.66) * mm, "end": v(8.4, -124.72) * mm});
            skLineSegment(sketch, "E31.37.1", {"start": v(14.7, -139.22) * mm, "end": v(13.38, -124.28) * mm});
            skLineSegment(sketch, "E31.37.2", {"start": v(14.7, -139.22) * mm, "end": v(9.7, -139.66) * mm});
            skLineSegment(sketch, "E31.37.4", {"start": v(13.38, -124.28) * mm, "end": v(8.4, -124.72) * mm});
            skLineSegment(sketch, "E31.38.0", {"start": v(21.84, -138.28) * mm, "end": v(19.24, -123.51) * mm});
            skLineSegment(sketch, "E31.38.1", {"start": v(26.77, -137.41) * mm, "end": v(24.16, -122.64) * mm});
            skLineSegment(sketch, "E31.38.2", {"start": v(26.77, -137.41) * mm, "end": v(21.84, -138.28) * mm});
            skLineSegment(sketch, "E31.38.4", {"start": v(24.16, -122.64) * mm, "end": v(19.24, -123.51) * mm});
            skLineSegment(sketch, "E31.39.0", {"start": v(33.81, -135.85) * mm, "end": v(29.93, -121.36) * mm});
            skLineSegment(sketch, "E31.39.1", {"start": v(38.64, -134.56) * mm, "end": v(34.76, -120.07) * mm});
            skLineSegment(sketch, "E31.39.2", {"start": v(38.64, -134.56) * mm, "end": v(33.81, -135.85) * mm});
            skLineSegment(sketch, "E31.39.4", {"start": v(34.76, -120.07) * mm, "end": v(29.93, -121.36) * mm});
            skLineSegment(sketch, "E31.40.0", {"start": v(45.53, -132.39) * mm, "end": v(40.4, -118.3) * mm});
            skLineSegment(sketch, "E31.40.1", {"start": v(50.22, -130.68) * mm, "end": v(45.1, -116.58) * mm});
            skLineSegment(sketch, "E31.40.2", {"start": v(50.22, -130.68) * mm, "end": v(45.53, -132.39) * mm});
            skLineSegment(sketch, "E31.40.4", {"start": v(45.1, -116.58) * mm, "end": v(40.4, -118.3) * mm});
            skLineSegment(sketch, "E31.41.0", {"start": v(56.9, -127.92) * mm, "end": v(50.55, -114.32) * mm});
            skLineSegment(sketch, "E31.41.1", {"start": v(61.42, -125.8) * mm, "end": v(55.08, -112.2) * mm});
            skLineSegment(sketch, "E31.41.2", {"start": v(61.42, -125.8) * mm, "end": v(56.9, -127.92) * mm});
            skLineSegment(sketch, "E31.41.4", {"start": v(55.08, -112.2) * mm, "end": v(50.55, -114.32) * mm});
            skLineSegment(sketch, "E31.42.0", {"start": v(67.82, -122.47) * mm, "end": v(60.32, -109.48) * mm});
            skLineSegment(sketch, "E31.42.1", {"start": v(72.15, -119.97) * mm, "end": v(64.65, -106.98) * mm});
            skLineSegment(sketch, "E31.42.2", {"start": v(72.15, -119.97) * mm, "end": v(67.82, -122.47) * mm});
            skLineSegment(sketch, "E31.42.4", {"start": v(64.65, -106.98) * mm, "end": v(60.32, -109.48) * mm});
            skLineSegment(sketch, "E31.43.0", {"start": v(78.24, -116.1) * mm, "end": v(69.63, -103.8) * mm});
            skLineSegment(sketch, "E31.43.1", {"start": v(82.33, -113.23) * mm, "end": v(73.73, -100.94) * mm});
            skLineSegment(sketch, "E31.43.2", {"start": v(82.33, -113.23) * mm, "end": v(78.24, -116.1) * mm});
            skLineSegment(sketch, "E31.43.4", {"start": v(73.73, -100.94) * mm, "end": v(69.63, -103.8) * mm});
            skLineSegment(sketch, "E31.44.0", {"start": v(88.06, -108.83) * mm, "end": v(78.42, -97.34) * mm});
            skLineSegment(sketch, "E31.44.1", {"start": v(91.89, -105.62) * mm, "end": v(82.25, -94.13) * mm});
            skLineSegment(sketch, "E31.44.2", {"start": v(91.89, -105.62) * mm, "end": v(88.06, -108.83) * mm});
            skLineSegment(sketch, "E31.44.4", {"start": v(82.25, -94.13) * mm, "end": v(78.42, -97.34) * mm});
            skLineSegment(sketch, "E31.45.0", {"start": v(97.2, -100.74) * mm, "end": v(86.6, -90.14) * mm});
            skLineSegment(sketch, "E31.45.1", {"start": v(100.75, -97.2) * mm, "end": v(90.14, -86.6) * mm});
            skLineSegment(sketch, "E31.45.2", {"start": v(100.75, -97.2) * mm, "end": v(97.2, -100.74) * mm});
            skLineSegment(sketch, "E31.45.4", {"start": v(90.14, -86.6) * mm, "end": v(86.6, -90.14) * mm});
            skLineSegment(sketch, "E31.46.0", {"start": v(105.62, -91.89) * mm, "end": v(94.13, -82.25) * mm});
            skLineSegment(sketch, "E31.46.1", {"start": v(108.83, -88.06) * mm, "end": v(97.34, -78.42) * mm});
            skLineSegment(sketch, "E31.46.2", {"start": v(108.83, -88.06) * mm, "end": v(105.62, -91.89) * mm});
            skLineSegment(sketch, "E31.46.4", {"start": v(97.34, -78.42) * mm, "end": v(94.13, -82.25) * mm});
            skLineSegment(sketch, "E31.47.0", {"start": v(113.23, -82.33) * mm, "end": v(100.94, -73.73) * mm});
            skLineSegment(sketch, "E31.47.1", {"start": v(116.1, -78.24) * mm, "end": v(103.8, -69.63) * mm});
            skLineSegment(sketch, "E31.47.2", {"start": v(116.1, -78.24) * mm, "end": v(113.23, -82.33) * mm});
            skLineSegment(sketch, "E31.47.4", {"start": v(103.8, -69.63) * mm, "end": v(100.94, -73.73) * mm});
            skLineSegment(sketch, "E31.48.0", {"start": v(119.97, -72.15) * mm, "end": v(106.98, -64.65) * mm});
            skLineSegment(sketch, "E31.48.1", {"start": v(122.47, -67.82) * mm, "end": v(109.48, -60.32) * mm});
            skLineSegment(sketch, "E31.48.2", {"start": v(122.47, -67.82) * mm, "end": v(119.97, -72.15) * mm});
            skLineSegment(sketch, "E31.48.4", {"start": v(109.48, -60.32) * mm, "end": v(106.98, -64.65) * mm});
            skLineSegment(sketch, "E31.49.0", {"start": v(125.8, -61.42) * mm, "end": v(112.2, -55.08) * mm});
            skLineSegment(sketch, "E31.49.1", {"start": v(127.92, -56.9) * mm, "end": v(114.32, -50.55) * mm});
            skLineSegment(sketch, "E31.49.2", {"start": v(127.92, -56.9) * mm, "end": v(125.8, -61.42) * mm});
            skLineSegment(sketch, "E31.49.4", {"start": v(114.32, -50.55) * mm, "end": v(112.2, -55.08) * mm});
            skLineSegment(sketch, "E31.50.0", {"start": v(130.68, -50.22) * mm, "end": v(116.58, -45.1) * mm});
            skLineSegment(sketch, "E31.50.1", {"start": v(132.39, -45.53) * mm, "end": v(118.3, -40.4) * mm});
            skLineSegment(sketch, "E31.50.2", {"start": v(132.39, -45.53) * mm, "end": v(130.68, -50.22) * mm});
            skLineSegment(sketch, "E31.50.4", {"start": v(118.3, -40.4) * mm, "end": v(116.58, -45.1) * mm});
            skLineSegment(sketch, "E31.51.0", {"start": v(134.56, -38.64) * mm, "end": v(120.07, -34.76) * mm});
            skLineSegment(sketch, "E31.51.1", {"start": v(135.85, -33.81) * mm, "end": v(121.36, -29.93) * mm});
            skLineSegment(sketch, "E31.51.2", {"start": v(135.85, -33.81) * mm, "end": v(134.56, -38.64) * mm});
            skLineSegment(sketch, "E31.51.4", {"start": v(121.36, -29.93) * mm, "end": v(120.07, -34.76) * mm});
            skLineSegment(sketch, "E31.52.0", {"start": v(137.41, -26.77) * mm, "end": v(122.64, -24.16) * mm});
            skLineSegment(sketch, "E31.52.1", {"start": v(138.28, -21.84) * mm, "end": v(123.51, -19.24) * mm});
            skLineSegment(sketch, "E31.52.2", {"start": v(138.28, -21.84) * mm, "end": v(137.41, -26.77) * mm});
            skLineSegment(sketch, "E31.52.4", {"start": v(123.51, -19.24) * mm, "end": v(122.64, -24.16) * mm});
            skLineSegment(sketch, "E31.53.0", {"start": v(139.22, -14.69) * mm, "end": v(124.28, -13.38) * mm});
            skLineSegment(sketch, "E31.53.1", {"start": v(139.66, -9.7) * mm, "end": v(124.72, -8.4) * mm});
            skLineSegment(sketch, "E31.53.2", {"start": v(139.66, -9.7) * mm, "end": v(139.22, -14.69) * mm});
            skLineSegment(sketch, "E31.53.4", {"start": v(124.72, -8.4) * mm, "end": v(124.28, -13.38) * mm});
            skLineSegment(sketch, "E31.54.0", {"start": v(139.98, -2.5) * mm, "end": v(124.98, -2.5) * mm});
            skLineSegment(sketch, "E31.54.1", {"start": v(139.98, 2.5) * mm, "end": v(124.98, 2.5) * mm});
            skLineSegment(sketch, "E31.54.2", {"start": v(139.98, 2.5) * mm, "end": v(139.98, -2.5) * mm});
            skLineSegment(sketch, "E31.54.4", {"start": v(124.98, 2.5) * mm, "end": v(124.98, -2.5) * mm});
            skLineSegment(sketch, "E31.55.0", {"start": v(139.66, 9.7) * mm, "end": v(124.72, 8.4) * mm});
            skLineSegment(sketch, "E31.55.1", {"start": v(139.22, 14.7) * mm, "end": v(124.28, 13.38) * mm});
            skLineSegment(sketch, "E31.55.2", {"start": v(139.22, 14.7) * mm, "end": v(139.66, 9.7) * mm});
            skLineSegment(sketch, "E31.55.4", {"start": v(124.28, 13.38) * mm, "end": v(124.72, 8.4) * mm});
            skLineSegment(sketch, "E31.56.0", {"start": v(138.28, 21.84) * mm, "end": v(123.51, 19.24) * mm});
            skLineSegment(sketch, "E31.56.1", {"start": v(137.41, 26.77) * mm, "end": v(122.64, 24.16) * mm});
            skLineSegment(sketch, "E31.56.2", {"start": v(137.41, 26.77) * mm, "end": v(138.28, 21.84) * mm});
            skLineSegment(sketch, "E31.56.4", {"start": v(122.64, 24.16) * mm, "end": v(123.51, 19.24) * mm});
            skLineSegment(sketch, "E31.57.0", {"start": v(135.85, 33.81) * mm, "end": v(121.36, 29.93) * mm});
            skLineSegment(sketch, "E31.57.1", {"start": v(134.56, 38.64) * mm, "end": v(120.07, 34.76) * mm});
            skLineSegment(sketch, "E31.57.2", {"start": v(134.56, 38.64) * mm, "end": v(135.85, 33.81) * mm});
            skLineSegment(sketch, "E31.57.4", {"start": v(120.07, 34.76) * mm, "end": v(121.36, 29.93) * mm});
            skLineSegment(sketch, "E31.58.0", {"start": v(132.39, 45.53) * mm, "end": v(118.3, 40.4) * mm});
            skLineSegment(sketch, "E31.58.1", {"start": v(130.68, 50.22) * mm, "end": v(116.58, 45.1) * mm});
            skLineSegment(sketch, "E31.58.2", {"start": v(130.68, 50.22) * mm, "end": v(132.39, 45.53) * mm});
            skLineSegment(sketch, "E31.58.4", {"start": v(116.58, 45.1) * mm, "end": v(118.3, 40.4) * mm});
            skLineSegment(sketch, "E31.59.0", {"start": v(127.92, 56.9) * mm, "end": v(114.32, 50.55) * mm});
            skLineSegment(sketch, "E31.59.1", {"start": v(125.8, 61.42) * mm, "end": v(112.2, 55.08) * mm});
            skLineSegment(sketch, "E31.59.2", {"start": v(125.8, 61.42) * mm, "end": v(127.92, 56.9) * mm});
            skLineSegment(sketch, "E31.59.4", {"start": v(112.2, 55.08) * mm, "end": v(114.32, 50.55) * mm});
            skLineSegment(sketch, "E31.60.0", {"start": v(122.47, 67.82) * mm, "end": v(109.48, 60.32) * mm});
            skLineSegment(sketch, "E31.60.1", {"start": v(119.97, 72.15) * mm, "end": v(106.98, 64.65) * mm});
            skLineSegment(sketch, "E31.60.2", {"start": v(119.97, 72.15) * mm, "end": v(122.47, 67.82) * mm});
            skLineSegment(sketch, "E31.60.4", {"start": v(106.98, 64.65) * mm, "end": v(109.48, 60.32) * mm});
            skLineSegment(sketch, "E31.61.0", {"start": v(116.1, 78.24) * mm, "end": v(103.8, 69.63) * mm});
            skLineSegment(sketch, "E31.61.1", {"start": v(113.23, 82.33) * mm, "end": v(100.94, 73.73) * mm});
            skLineSegment(sketch, "E31.61.2", {"start": v(113.23, 82.33) * mm, "end": v(116.1, 78.24) * mm});
            skLineSegment(sketch, "E31.61.4", {"start": v(100.94, 73.73) * mm, "end": v(103.8, 69.63) * mm});
            skLineSegment(sketch, "E31.62.0", {"start": v(108.83, 88.06) * mm, "end": v(97.34, 78.42) * mm});
            skLineSegment(sketch, "E31.62.1", {"start": v(105.62, 91.89) * mm, "end": v(94.13, 82.25) * mm});
            skLineSegment(sketch, "E31.62.2", {"start": v(105.62, 91.89) * mm, "end": v(108.83, 88.06) * mm});
            skLineSegment(sketch, "E31.62.4", {"start": v(94.13, 82.25) * mm, "end": v(97.34, 78.42) * mm});
            skLineSegment(sketch, "E31.63.0", {"start": v(100.74, 97.2) * mm, "end": v(90.14, 86.6) * mm});
            skLineSegment(sketch, "E31.63.1", {"start": v(97.2, 100.75) * mm, "end": v(86.6, 90.14) * mm});
            skLineSegment(sketch, "E31.63.2", {"start": v(97.2, 100.75) * mm, "end": v(100.74, 97.2) * mm});
            skLineSegment(sketch, "E31.63.4", {"start": v(86.6, 90.14) * mm, "end": v(90.14, 86.6) * mm});
            skLineSegment(sketch, "E31.64.0", {"start": v(91.89, 105.62) * mm, "end": v(82.25, 94.13) * mm});
            skLineSegment(sketch, "E31.64.1", {"start": v(88.06, 108.83) * mm, "end": v(78.42, 97.34) * mm});
            skLineSegment(sketch, "E31.64.2", {"start": v(88.06, 108.83) * mm, "end": v(91.89, 105.62) * mm});
            skLineSegment(sketch, "E31.64.4", {"start": v(78.42, 97.34) * mm, "end": v(82.25, 94.13) * mm});
            skLineSegment(sketch, "E31.65.0", {"start": v(82.33, 113.23) * mm, "end": v(73.73, 100.94) * mm});
            skLineSegment(sketch, "E31.65.1", {"start": v(78.24, 116.1) * mm, "end": v(69.63, 103.8) * mm});
            skLineSegment(sketch, "E31.65.2", {"start": v(78.24, 116.1) * mm, "end": v(82.33, 113.23) * mm});
            skLineSegment(sketch, "E31.65.4", {"start": v(69.63, 103.8) * mm, "end": v(73.73, 100.94) * mm});
            skLineSegment(sketch, "E31.66.0", {"start": v(72.15, 119.97) * mm, "end": v(64.65, 106.98) * mm});
            skLineSegment(sketch, "E31.66.1", {"start": v(67.82, 122.47) * mm, "end": v(60.32, 109.48) * mm});
            skLineSegment(sketch, "E31.66.2", {"start": v(67.82, 122.47) * mm, "end": v(72.15, 119.97) * mm});
            skLineSegment(sketch, "E31.66.4", {"start": v(60.32, 109.48) * mm, "end": v(64.65, 106.98) * mm});
            skLineSegment(sketch, "E31.67.0", {"start": v(61.42, 125.8) * mm, "end": v(55.08, 112.2) * mm});
            skLineSegment(sketch, "E31.67.1", {"start": v(56.9, 127.92) * mm, "end": v(50.55, 114.32) * mm});
            skLineSegment(sketch, "E31.67.2", {"start": v(56.9, 127.92) * mm, "end": v(61.42, 125.8) * mm});
            skLineSegment(sketch, "E31.67.4", {"start": v(50.55, 114.32) * mm, "end": v(55.08, 112.2) * mm});
            skLineSegment(sketch, "E31.68.0", {"start": v(50.22, 130.68) * mm, "end": v(45.1, 116.58) * mm});
            skLineSegment(sketch, "E31.68.1", {"start": v(45.53, 132.39) * mm, "end": v(40.4, 118.3) * mm});
            skLineSegment(sketch, "E31.68.2", {"start": v(45.53, 132.39) * mm, "end": v(50.22, 130.68) * mm});
            skLineSegment(sketch, "E31.68.4", {"start": v(40.4, 118.3) * mm, "end": v(45.1, 116.58) * mm});
            skLineSegment(sketch, "E31.69.0", {"start": v(38.64, 134.56) * mm, "end": v(34.76, 120.07) * mm});
            skLineSegment(sketch, "E31.69.1", {"start": v(33.81, 135.85) * mm, "end": v(29.93, 121.36) * mm});
            skLineSegment(sketch, "E31.69.2", {"start": v(33.81, 135.85) * mm, "end": v(38.64, 134.56) * mm});
            skLineSegment(sketch, "E31.69.4", {"start": v(29.93, 121.36) * mm, "end": v(34.76, 120.07) * mm});
            skLineSegment(sketch, "E31.70.0", {"start": v(26.77, 137.41) * mm, "end": v(24.16, 122.64) * mm});
            skLineSegment(sketch, "E31.70.1", {"start": v(21.84, 138.28) * mm, "end": v(19.24, 123.51) * mm});
            skLineSegment(sketch, "E31.70.2", {"start": v(21.84, 138.28) * mm, "end": v(26.77, 137.41) * mm});
            skLineSegment(sketch, "E31.70.4", {"start": v(19.24, 123.51) * mm, "end": v(24.16, 122.64) * mm});
            skLineSegment(sketch, "E31.71.0", {"start": v(14.69, 139.22) * mm, "end": v(13.38, 124.28) * mm});
            skLineSegment(sketch, "E31.71.1", {"start": v(9.7, 139.66) * mm, "end": v(8.4, 124.72) * mm});
            skLineSegment(sketch, "E31.71.2", {"start": v(9.7, 139.66) * mm, "end": v(14.69, 139.22) * mm});
            skLineSegment(sketch, "E31.71.4", {"start": v(8.4, 124.72) * mm, "end": v(13.38, 124.28) * mm});
            skSolve(sketch);
        }
        {
            var Q0;
            Q0=makeQuery(id+"F6.imprint","IMPRINT",FACE,{"disambiguationData":[TD([[makeQuery(id+"F6.imprint","IMPRINT",EDGE,{"derivedFrom":sQuery(id+"F6.wireOp",EDGE,"E30.bottom")}),-1.0]])]});
            var Q1;
            {var subQ0=sQuery(id+"F6.wireOp",EDGE,"E31.71.0");Q1=makeQuery(id+"F6.imprint","IMPRINT",FACE,{"disambiguationData":[TD([[makeQuery(id+"F6.imprint","IMPRINT",EDGE,{"derivedFrom":subQ0}),-1.0]])]});}
            var Q2;
            {var subQ0=sQuery(id+"F6.wireOp",EDGE,"E31.70.0");Q2=makeQuery(id+"F6.imprint","IMPRINT",FACE,{"disambiguationData":[TD([[makeQuery(id+"F6.imprint","IMPRINT",EDGE,{"derivedFrom":subQ0}),-1.0]])]});}
            var Q3;
            {var subQ0=sQuery(id+"F6.wireOp",EDGE,"E31.69.0");Q3=makeQuery(id+"F6.imprint","IMPRINT",FACE,{"disambiguationData":[TD([[makeQuery(id+"F6.imprint","IMPRINT",EDGE,{"derivedFrom":subQ0}),-1.0]])]});}
            var Q4;
            {var subQ0=sQuery(id+"F6.wireOp",EDGE,"E31.68.0");Q4=makeQuery(id+"F6.imprint","IMPRINT",FACE,{"disambiguationData":[TD([[makeQuery(id+"F6.imprint","IMPRINT",EDGE,{"derivedFrom":subQ0}),-1.0]])]});}
            var Q5;
            {var subQ0=sQuery(id+"F6.wireOp",EDGE,"E31.67.0");Q5=makeQuery(id+"F6.imprint","IMPRINT",FACE,{"disambiguationData":[TD([[makeQuery(id+"F6.imprint","IMPRINT",EDGE,{"derivedFrom":subQ0}),-1.0]])]});}
            var Q6;
            {var subQ0=sQuery(id+"F6.wireOp",EDGE,"E31.66.0");Q6=makeQuery(id+"F6.imprint","IMPRINT",FACE,{"disambiguationData":[TD([[makeQuery(id+"F6.imprint","IMPRINT",EDGE,{"derivedFrom":subQ0}),-1.0]])]});}
            var Q7;
            {var subQ0=sQuery(id+"F6.wireOp",EDGE,"E31.65.0");Q7=makeQuery(id+"F6.imprint","IMPRINT",FACE,{"disambiguationData":[TD([[makeQuery(id+"F6.imprint","IMPRINT",EDGE,{"derivedFrom":subQ0}),-1.0]])]});}
            var Q8;
            {var subQ0=sQuery(id+"F6.wireOp",EDGE,"E31.64.0");Q8=makeQuery(id+"F6.imprint","IMPRINT",FACE,{"disambiguationData":[TD([[makeQuery(id+"F6.imprint","IMPRINT",EDGE,{"derivedFrom":subQ0}),-1.0]])]});}
            var Q9;
            {var subQ0=sQuery(id+"F6.wireOp",EDGE,"E31.63.0");Q9=makeQuery(id+"F6.imprint","IMPRINT",FACE,{"disambiguationData":[TD([[makeQuery(id+"F6.imprint","IMPRINT",EDGE,{"derivedFrom":subQ0}),-1.0]])]});}
            var Q10;
            {var subQ0=sQuery(id+"F6.wireOp",EDGE,"E31.62.0");Q10=makeQuery(id+"F6.imprint","IMPRINT",FACE,{"disambiguationData":[TD([[makeQuery(id+"F6.imprint","IMPRINT",EDGE,{"derivedFrom":subQ0}),-1.0]])]});}
            var Q11;
            {var subQ0=sQuery(id+"F6.wireOp",EDGE,"E31.61.0");Q11=makeQuery(id+"F6.imprint","IMPRINT",FACE,{"disambiguationData":[TD([[makeQuery(id+"F6.imprint","IMPRINT",EDGE,{"derivedFrom":subQ0}),-1.0]])]});}
            var Q12;
            {var subQ0=sQuery(id+"F6.wireOp",EDGE,"E31.60.0");Q12=makeQuery(id+"F6.imprint","IMPRINT",FACE,{"disambiguationData":[TD([[makeQuery(id+"F6.imprint","IMPRINT",EDGE,{"derivedFrom":subQ0}),-1.0]])]});}
            var Q13;
            {var subQ0=sQuery(id+"F6.wireOp",EDGE,"E31.59.0");Q13=makeQuery(id+"F6.imprint","IMPRINT",FACE,{"disambiguationData":[TD([[makeQuery(id+"F6.imprint","IMPRINT",EDGE,{"derivedFrom":subQ0}),-1.0]])]});}
            var Q14;
            {var subQ0=sQuery(id+"F6.wireOp",EDGE,"E31.58.0");Q14=makeQuery(id+"F6.imprint","IMPRINT",FACE,{"disambiguationData":[TD([[makeQuery(id+"F6.imprint","IMPRINT",EDGE,{"derivedFrom":subQ0}),-1.0]])]});}
            var Q15;
            {var subQ0=sQuery(id+"F6.wireOp",EDGE,"E31.57.0");Q15=makeQuery(id+"F6.imprint","IMPRINT",FACE,{"disambiguationData":[TD([[makeQuery(id+"F6.imprint","IMPRINT",EDGE,{"derivedFrom":subQ0}),-1.0]])]});}
            var Q16;
            {var subQ0=sQuery(id+"F6.wireOp",EDGE,"E31.56.0");Q16=makeQuery(id+"F6.imprint","IMPRINT",FACE,{"disambiguationData":[TD([[makeQuery(id+"F6.imprint","IMPRINT",EDGE,{"derivedFrom":subQ0}),-1.0]])]});}
            var Q17;
            {var subQ0=sQuery(id+"F6.wireOp",EDGE,"E31.55.0");Q17=makeQuery(id+"F6.imprint","IMPRINT",FACE,{"disambiguationData":[TD([[makeQuery(id+"F6.imprint","IMPRINT",EDGE,{"derivedFrom":subQ0}),-1.0]])]});}
            var Q18;
            {var subQ0=sQuery(id+"F6.wireOp",EDGE,"E31.54.0");Q18=makeQuery(id+"F6.imprint","IMPRINT",FACE,{"disambiguationData":[TD([[makeQuery(id+"F6.imprint","IMPRINT",EDGE,{"derivedFrom":subQ0}),-1.0]])]});}
            var Q19;
            {var subQ0=sQuery(id+"F6.wireOp",EDGE,"E31.53.0");Q19=makeQuery(id+"F6.imprint","IMPRINT",FACE,{"disambiguationData":[TD([[makeQuery(id+"F6.imprint","IMPRINT",EDGE,{"derivedFrom":subQ0}),-1.0]])]});}
            var Q20;
            {var subQ0=sQuery(id+"F6.wireOp",EDGE,"E31.52.0");Q20=makeQuery(id+"F6.imprint","IMPRINT",FACE,{"disambiguationData":[TD([[makeQuery(id+"F6.imprint","IMPRINT",EDGE,{"derivedFrom":subQ0}),-1.0]])]});}
            var Q21;
            {var subQ0=sQuery(id+"F6.wireOp",EDGE,"E31.51.0");Q21=makeQuery(id+"F6.imprint","IMPRINT",FACE,{"disambiguationData":[TD([[makeQuery(id+"F6.imprint","IMPRINT",EDGE,{"derivedFrom":subQ0}),-1.0]])]});}
            var Q22;
            {var subQ0=sQuery(id+"F6.wireOp",EDGE,"E31.49.0");Q22=makeQuery(id+"F6.imprint","IMPRINT",FACE,{"disambiguationData":[TD([[makeQuery(id+"F6.imprint","IMPRINT",EDGE,{"derivedFrom":subQ0}),-1.0]])]});}
            var Q23;
            {var subQ0=sQuery(id+"F6.wireOp",EDGE,"E31.50.0");Q23=makeQuery(id+"F6.imprint","IMPRINT",FACE,{"disambiguationData":[TD([[makeQuery(id+"F6.imprint","IMPRINT",EDGE,{"derivedFrom":subQ0}),-1.0]])]});}
            var Q24;
            {var subQ0=sQuery(id+"F6.wireOp",EDGE,"E31.48.0");Q24=makeQuery(id+"F6.imprint","IMPRINT",FACE,{"disambiguationData":[TD([[makeQuery(id+"F6.imprint","IMPRINT",EDGE,{"derivedFrom":subQ0}),-1.0]])]});}
            var Q25;
            {var subQ0=sQuery(id+"F6.wireOp",EDGE,"E31.47.0");Q25=makeQuery(id+"F6.imprint","IMPRINT",FACE,{"disambiguationData":[TD([[makeQuery(id+"F6.imprint","IMPRINT",EDGE,{"derivedFrom":subQ0}),-1.0]])]});}
            var Q26;
            {var subQ0=sQuery(id+"F6.wireOp",EDGE,"E31.46.0");Q26=makeQuery(id+"F6.imprint","IMPRINT",FACE,{"disambiguationData":[TD([[makeQuery(id+"F6.imprint","IMPRINT",EDGE,{"derivedFrom":subQ0}),-1.0]])]});}
            var Q27;
            {var subQ0=sQuery(id+"F6.wireOp",EDGE,"E31.45.0");Q27=makeQuery(id+"F6.imprint","IMPRINT",FACE,{"disambiguationData":[TD([[makeQuery(id+"F6.imprint","IMPRINT",EDGE,{"derivedFrom":subQ0}),-1.0]])]});}
            var Q28;
            {var subQ0=sQuery(id+"F6.wireOp",EDGE,"E31.44.0");Q28=makeQuery(id+"F6.imprint","IMPRINT",FACE,{"disambiguationData":[TD([[makeQuery(id+"F6.imprint","IMPRINT",EDGE,{"derivedFrom":subQ0}),-1.0]])]});}
            var Q29;
            {var subQ0=sQuery(id+"F6.wireOp",EDGE,"E31.43.0");Q29=makeQuery(id+"F6.imprint","IMPRINT",FACE,{"disambiguationData":[TD([[makeQuery(id+"F6.imprint","IMPRINT",EDGE,{"derivedFrom":subQ0}),-1.0]])]});}
            var Q30;
            {var subQ0=sQuery(id+"F6.wireOp",EDGE,"E31.42.0");Q30=makeQuery(id+"F6.imprint","IMPRINT",FACE,{"disambiguationData":[TD([[makeQuery(id+"F6.imprint","IMPRINT",EDGE,{"derivedFrom":subQ0}),-1.0]])]});}
            var Q31;
            {var subQ0=sQuery(id+"F6.wireOp",EDGE,"E31.40.0");Q31=makeQuery(id+"F6.imprint","IMPRINT",FACE,{"disambiguationData":[TD([[makeQuery(id+"F6.imprint","IMPRINT",EDGE,{"derivedFrom":subQ0}),-1.0]])]});}
            var Q32;
            {var subQ0=sQuery(id+"F6.wireOp",EDGE,"E31.39.0");Q32=makeQuery(id+"F6.imprint","IMPRINT",FACE,{"disambiguationData":[TD([[makeQuery(id+"F6.imprint","IMPRINT",EDGE,{"derivedFrom":subQ0}),-1.0]])]});}
            var Q33;
            {var subQ0=sQuery(id+"F6.wireOp",EDGE,"E31.38.0");Q33=makeQuery(id+"F6.imprint","IMPRINT",FACE,{"disambiguationData":[TD([[makeQuery(id+"F6.imprint","IMPRINT",EDGE,{"derivedFrom":subQ0}),-1.0]])]});}
            var Q34;
            {var subQ0=sQuery(id+"F6.wireOp",EDGE,"E31.37.0");Q34=makeQuery(id+"F6.imprint","IMPRINT",FACE,{"disambiguationData":[TD([[makeQuery(id+"F6.imprint","IMPRINT",EDGE,{"derivedFrom":subQ0}),-1.0]])]});}
            var Q35;
            {var subQ0=sQuery(id+"F6.wireOp",EDGE,"E31.36.0");Q35=makeQuery(id+"F6.imprint","IMPRINT",FACE,{"disambiguationData":[TD([[makeQuery(id+"F6.imprint","IMPRINT",EDGE,{"derivedFrom":subQ0}),-1.0]])]});}
            var Q36;
            {var subQ0=sQuery(id+"F6.wireOp",EDGE,"E31.35.0");Q36=makeQuery(id+"F6.imprint","IMPRINT",FACE,{"disambiguationData":[TD([[makeQuery(id+"F6.imprint","IMPRINT",EDGE,{"derivedFrom":subQ0}),-1.0]])]});}
            var Q37;
            {var subQ0=sQuery(id+"F6.wireOp",EDGE,"E31.34.0");Q37=makeQuery(id+"F6.imprint","IMPRINT",FACE,{"disambiguationData":[TD([[makeQuery(id+"F6.imprint","IMPRINT",EDGE,{"derivedFrom":subQ0}),-1.0]])]});}
            var Q38;
            {var subQ0=sQuery(id+"F6.wireOp",EDGE,"E31.41.0");Q38=makeQuery(id+"F6.imprint","IMPRINT",FACE,{"disambiguationData":[TD([[makeQuery(id+"F6.imprint","IMPRINT",EDGE,{"derivedFrom":subQ0}),-1.0]])]});}
            var Q39;
            {var subQ0=sQuery(id+"F6.wireOp",EDGE,"E31.33.0");Q39=makeQuery(id+"F6.imprint","IMPRINT",FACE,{"disambiguationData":[TD([[makeQuery(id+"F6.imprint","IMPRINT",EDGE,{"derivedFrom":subQ0}),-1.0]])]});}
            var Q40;
            {var subQ0=sQuery(id+"F6.wireOp",EDGE,"E31.32.0");Q40=makeQuery(id+"F6.imprint","IMPRINT",FACE,{"disambiguationData":[TD([[makeQuery(id+"F6.imprint","IMPRINT",EDGE,{"derivedFrom":subQ0}),-1.0]])]});}
            var Q41;
            {var subQ0=sQuery(id+"F6.wireOp",EDGE,"E31.31.0");Q41=makeQuery(id+"F6.imprint","IMPRINT",FACE,{"disambiguationData":[TD([[makeQuery(id+"F6.imprint","IMPRINT",EDGE,{"derivedFrom":subQ0}),-1.0]])]});}
            var Q42;
            {var subQ0=sQuery(id+"F6.wireOp",EDGE,"E31.30.0");Q42=makeQuery(id+"F6.imprint","IMPRINT",FACE,{"disambiguationData":[TD([[makeQuery(id+"F6.imprint","IMPRINT",EDGE,{"derivedFrom":subQ0}),-1.0]])]});}
            var Q43;
            {var subQ0=sQuery(id+"F6.wireOp",EDGE,"E31.29.0");Q43=makeQuery(id+"F6.imprint","IMPRINT",FACE,{"disambiguationData":[TD([[makeQuery(id+"F6.imprint","IMPRINT",EDGE,{"derivedFrom":subQ0}),-1.0]])]});}
            var Q44;
            {var subQ0=sQuery(id+"F6.wireOp",EDGE,"E31.28.0");Q44=makeQuery(id+"F6.imprint","IMPRINT",FACE,{"disambiguationData":[TD([[makeQuery(id+"F6.imprint","IMPRINT",EDGE,{"derivedFrom":subQ0}),-1.0]])]});}
            var Q45;
            {var subQ0=sQuery(id+"F6.wireOp",EDGE,"E31.27.0");Q45=makeQuery(id+"F6.imprint","IMPRINT",FACE,{"disambiguationData":[TD([[makeQuery(id+"F6.imprint","IMPRINT",EDGE,{"derivedFrom":subQ0}),-1.0]])]});}
            var Q46;
            {var subQ0=sQuery(id+"F6.wireOp",EDGE,"E31.26.0");Q46=makeQuery(id+"F6.imprint","IMPRINT",FACE,{"disambiguationData":[TD([[makeQuery(id+"F6.imprint","IMPRINT",EDGE,{"derivedFrom":subQ0}),-1.0]])]});}
            var Q47;
            {var subQ0=sQuery(id+"F6.wireOp",EDGE,"E31.24.0");Q47=makeQuery(id+"F6.imprint","IMPRINT",FACE,{"disambiguationData":[TD([[makeQuery(id+"F6.imprint","IMPRINT",EDGE,{"derivedFrom":subQ0}),-1.0]])]});}
            var Q48;
            {var subQ0=sQuery(id+"F6.wireOp",EDGE,"E31.23.0");Q48=makeQuery(id+"F6.imprint","IMPRINT",FACE,{"disambiguationData":[TD([[makeQuery(id+"F6.imprint","IMPRINT",EDGE,{"derivedFrom":subQ0}),-1.0]])]});}
            var Q49;
            {var subQ0=sQuery(id+"F6.wireOp",EDGE,"E31.25.0");Q49=makeQuery(id+"F6.imprint","IMPRINT",FACE,{"disambiguationData":[TD([[makeQuery(id+"F6.imprint","IMPRINT",EDGE,{"derivedFrom":subQ0}),-1.0]])]});}
            var Q50;
            {var subQ0=sQuery(id+"F6.wireOp",EDGE,"E31.22.0");Q50=makeQuery(id+"F6.imprint","IMPRINT",FACE,{"disambiguationData":[TD([[makeQuery(id+"F6.imprint","IMPRINT",EDGE,{"derivedFrom":subQ0}),-1.0]])]});}
            var Q51;
            {var subQ0=sQuery(id+"F6.wireOp",EDGE,"E31.21.0");Q51=makeQuery(id+"F6.imprint","IMPRINT",FACE,{"disambiguationData":[TD([[makeQuery(id+"F6.imprint","IMPRINT",EDGE,{"derivedFrom":subQ0}),-1.0]])]});}
            var Q52;
            {var subQ0=sQuery(id+"F6.wireOp",EDGE,"E31.20.0");Q52=makeQuery(id+"F6.imprint","IMPRINT",FACE,{"disambiguationData":[TD([[makeQuery(id+"F6.imprint","IMPRINT",EDGE,{"derivedFrom":subQ0}),-1.0]])]});}
            var Q53;
            {var subQ0=sQuery(id+"F6.wireOp",EDGE,"E31.19.0");Q53=makeQuery(id+"F6.imprint","IMPRINT",FACE,{"disambiguationData":[TD([[makeQuery(id+"F6.imprint","IMPRINT",EDGE,{"derivedFrom":subQ0}),-1.0]])]});}
            var Q54;
            {var subQ0=sQuery(id+"F6.wireOp",EDGE,"E31.18.0");Q54=makeQuery(id+"F6.imprint","IMPRINT",FACE,{"disambiguationData":[TD([[makeQuery(id+"F6.imprint","IMPRINT",EDGE,{"derivedFrom":subQ0}),-1.0]])]});}
            var Q55;
            {var subQ0=sQuery(id+"F6.wireOp",EDGE,"E31.17.0");Q55=makeQuery(id+"F6.imprint","IMPRINT",FACE,{"disambiguationData":[TD([[makeQuery(id+"F6.imprint","IMPRINT",EDGE,{"derivedFrom":subQ0}),-1.0]])]});}
            var Q56;
            {var subQ0=sQuery(id+"F6.wireOp",EDGE,"E31.16.0");Q56=makeQuery(id+"F6.imprint","IMPRINT",FACE,{"disambiguationData":[TD([[makeQuery(id+"F6.imprint","IMPRINT",EDGE,{"derivedFrom":subQ0}),-1.0]])]});}
            var Q57;
            {var subQ0=sQuery(id+"F6.wireOp",EDGE,"E31.14.0");Q57=makeQuery(id+"F6.imprint","IMPRINT",FACE,{"disambiguationData":[TD([[makeQuery(id+"F6.imprint","IMPRINT",EDGE,{"derivedFrom":subQ0}),-1.0]])]});}
            var Q58;
            {var subQ0=sQuery(id+"F6.wireOp",EDGE,"E31.13.0");Q58=makeQuery(id+"F6.imprint","IMPRINT",FACE,{"disambiguationData":[TD([[makeQuery(id+"F6.imprint","IMPRINT",EDGE,{"derivedFrom":subQ0}),-1.0]])]});}
            var Q59;
            {var subQ0=sQuery(id+"F6.wireOp",EDGE,"E31.12.0");Q59=makeQuery(id+"F6.imprint","IMPRINT",FACE,{"disambiguationData":[TD([[makeQuery(id+"F6.imprint","IMPRINT",EDGE,{"derivedFrom":subQ0}),-1.0]])]});}
            var Q60;
            {var subQ0=sQuery(id+"F6.wireOp",EDGE,"E31.1.0");Q60=makeQuery(id+"F6.imprint","IMPRINT",FACE,{"disambiguationData":[TD([[makeQuery(id+"F6.imprint","IMPRINT",EDGE,{"derivedFrom":subQ0}),-1.0]])]});}
            var Q61;
            {var subQ0=sQuery(id+"F6.wireOp",EDGE,"E31.2.0");Q61=makeQuery(id+"F6.imprint","IMPRINT",FACE,{"disambiguationData":[TD([[makeQuery(id+"F6.imprint","IMPRINT",EDGE,{"derivedFrom":subQ0}),-1.0]])]});}
            var Q62;
            {var subQ0=sQuery(id+"F6.wireOp",EDGE,"E31.4.0");Q62=makeQuery(id+"F6.imprint","IMPRINT",FACE,{"disambiguationData":[TD([[makeQuery(id+"F6.imprint","IMPRINT",EDGE,{"derivedFrom":subQ0}),-1.0]])]});}
            var Q63;
            {var subQ0=sQuery(id+"F6.wireOp",EDGE,"E31.5.0");Q63=makeQuery(id+"F6.imprint","IMPRINT",FACE,{"disambiguationData":[TD([[makeQuery(id+"F6.imprint","IMPRINT",EDGE,{"derivedFrom":subQ0}),-1.0]])]});}
            var Q64;
            {var subQ0=sQuery(id+"F6.wireOp",EDGE,"E31.3.0");Q64=makeQuery(id+"F6.imprint","IMPRINT",FACE,{"disambiguationData":[TD([[makeQuery(id+"F6.imprint","IMPRINT",EDGE,{"derivedFrom":subQ0}),-1.0]])]});}
            var Q65;
            {var subQ0=sQuery(id+"F6.wireOp",EDGE,"E31.6.0");Q65=makeQuery(id+"F6.imprint","IMPRINT",FACE,{"disambiguationData":[TD([[makeQuery(id+"F6.imprint","IMPRINT",EDGE,{"derivedFrom":subQ0}),-1.0]])]});}
            var Q66;
            {var subQ0=sQuery(id+"F6.wireOp",EDGE,"E31.7.0");Q66=makeQuery(id+"F6.imprint","IMPRINT",FACE,{"disambiguationData":[TD([[makeQuery(id+"F6.imprint","IMPRINT",EDGE,{"derivedFrom":subQ0}),-1.0]])]});}
            var Q67;
            {var subQ0=sQuery(id+"F6.wireOp",EDGE,"E31.8.0");Q67=makeQuery(id+"F6.imprint","IMPRINT",FACE,{"disambiguationData":[TD([[makeQuery(id+"F6.imprint","IMPRINT",EDGE,{"derivedFrom":subQ0}),-1.0]])]});}
            var Q68;
            {var subQ0=sQuery(id+"F6.wireOp",EDGE,"E31.9.0");Q68=makeQuery(id+"F6.imprint","IMPRINT",FACE,{"disambiguationData":[TD([[makeQuery(id+"F6.imprint","IMPRINT",EDGE,{"derivedFrom":subQ0}),-1.0]])]});}
            var Q69;
            {var subQ0=sQuery(id+"F6.wireOp",EDGE,"E31.10.0");Q69=makeQuery(id+"F6.imprint","IMPRINT",FACE,{"disambiguationData":[TD([[makeQuery(id+"F6.imprint","IMPRINT",EDGE,{"derivedFrom":subQ0}),-1.0]])]});}
            var Q70;
            {var subQ0=sQuery(id+"F6.wireOp",EDGE,"E31.11.0");Q70=makeQuery(id+"F6.imprint","IMPRINT",FACE,{"disambiguationData":[TD([[makeQuery(id+"F6.imprint","IMPRINT",EDGE,{"derivedFrom":subQ0}),-1.0]])]});}
            var Q71;
            {var subQ0=sQuery(id+"F6.wireOp",EDGE,"E31.15.0");Q71=makeQuery(id+"F6.imprint","IMPRINT",FACE,{"disambiguationData":[TD([[makeQuery(id+"F6.imprint","IMPRINT",EDGE,{"derivedFrom":subQ0}),-1.0]])]});}
            extrude(context, id + "F7", {"entities" : qUnion([Q0, Q1, Q2, Q3, Q4, Q5, Q6, Q7, Q8, Q9, Q10, Q11, Q12, Q13, Q14, Q15, Q16, Q17, Q18, Q19, Q20, Q21, Q22, Q23, Q24, Q25, Q26, Q27, Q28, Q29, Q30, Q31, Q32, Q33, Q34, Q35, Q36, Q37, Q38, Q39, Q40, Q41, Q42, Q43, Q44, Q45, Q46, Q47, Q48, Q49, Q50, Q51, Q52, Q53, Q54, Q55, Q56, Q57, Q58, Q59, Q60, Q61, Q62, Q63, Q64, Q65, Q66, Q67, Q68, Q69, Q70, Q71]), "operationType" : NewBodyOperationType.REMOVE, "oppositeDirection" : true, "depth" : 25 * mm});
        }
    });
